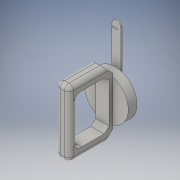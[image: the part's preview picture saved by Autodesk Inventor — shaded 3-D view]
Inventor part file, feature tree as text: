
AUTODESK INVENTOR PART (.ipt)
format: ipt  version: 2016 (Build 200138000, 138)  size: 207,872 bytes
history: native  units: mm
features: extrude x6, sketch x6, fillet x2, chamfer x1
ambient origin geometry x8: Origin, YZ Plane, XZ Plane, XY Plane, X Axis, Y Axis, Z Axis, Center Point
bodies: Solid1 (feature_tree)
feature tree (15):
  extrude  "Extrusion1"  Depth=20.0mm TaperAngle=0.0deg
  extrude  "Extrusion2"  Depth=150.0mm
  chamfer  "Chamfer2"  Distance=100.0mm
  extrude  "Extrusion7"  Depth=3.0mm TaperAngle=0.0deg
  fillet  "Fillet3"  Radius=3.0mm
  extrude  "Extrusion4"  Depth=20.0mm
  extrude  "Extrusion5"  Depth=20.0mm
  extrude  "Extrusion8"  Depth=10.0mm
  fillet  "Fillet4"  Radius=50.0mm
  sketch  "Sketch1"  dims[d0=100.0mm d1=20.0mm d2=0.0mm]
  sketch  "Sketch2"  dims[d5=100.0mm d6=150.0mm d7=100.0mm d8=0.0mm]
  sketch  "Sketch4"  dims[d21=20.0mm d22=3.0mm d23=0.0mm d28=3.0mm d29=0.0mm]
  sketch  "Sketch5"  dims[d36=20.0mm d37=2.0mm d38=45.0deg d39=20.0mm]
  sketch  "Sketch7"  dims[d40=20.0mm d41=20.0mm]
  sketch  "Sketch8"  dims[d42=15.0mm d43=8.726646mm d45=50.0mm d46=0.0mm d48=10.0mm d49=150.0mm d50=3.0mm d51=12.0mm d52=15.0mm d53=50.0mm d54=0.0mm d55=10.0mm]
